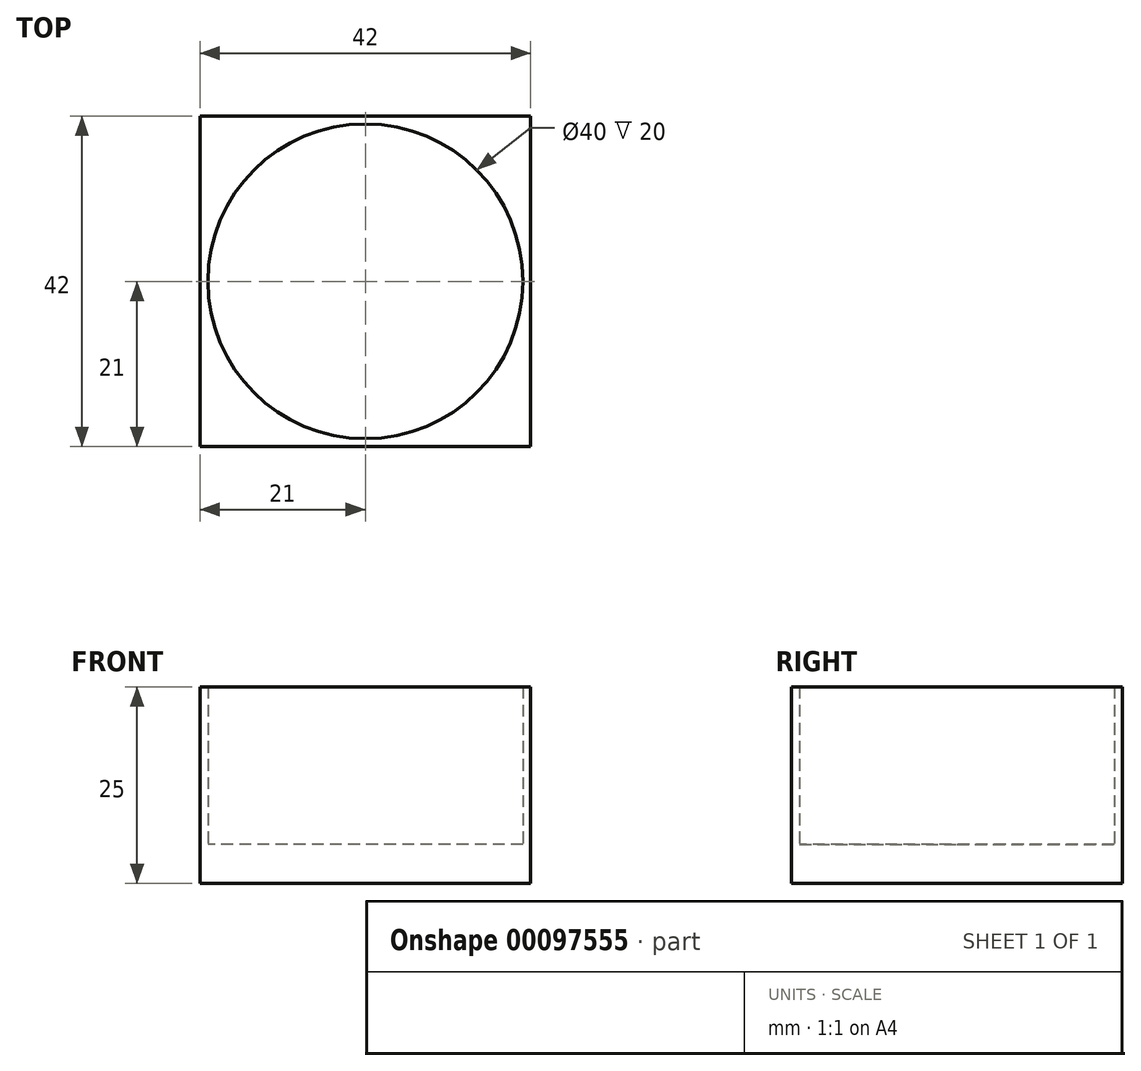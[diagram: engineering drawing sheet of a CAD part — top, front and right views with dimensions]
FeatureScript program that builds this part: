
annotation { "Feature Type Name" : "Feature", "Feature Type Description" : "" }
export const myFeature = defineFeature(function(context is Context, id is Id, definition is map)
    precondition{}
    {
        {
            var Q0;
            Q0=qCreatedBy(makeId("Top.planeOp"),FACE);
            var sketch = newSketch(context, id + "F0", { "sketchPlane" : qUnion([Q0])});
            skCircle(sketch, "E0", {"center": v(0, 0) * mm, "radius": 20 * mm});
            skLineSegment(sketch, "E1.bottom", {"start": v(0, 0) * mm, "end": v(-21, 0) * mm});
            skLineSegment(sketch, "E1.top", {"start": v(0, 0) * mm, "end": v(-21, 0) * mm});
            skLineSegment(sketch, "E1.left", {"start": v(0, 0) * mm, "end": v(0, 0) * mm});
            skLineSegment(sketch, "E1.right", {"start": v(-21, 0) * mm, "end": v(-21, 0) * mm});
            skLineSegment(sketch, "E2", {"start": v(-21, 0) * mm, "end": v(-21, 21) * mm});
            skLineSegment(sketch, "E3.bottom", {"start": v(-21, 21) * mm, "end": v(21, 21) * mm});
            skLineSegment(sketch, "E3.top", {"start": v(-21, -21) * mm, "end": v(21, -21) * mm});
            skLineSegment(sketch, "E3.left", {"start": v(-21, 21) * mm, "end": v(-21, -21) * mm});
            skLineSegment(sketch, "E3.right", {"start": v(21, 21) * mm, "end": v(21, -21) * mm});
            skSolve(sketch);
        }
        {
            var Q0;
            Q0=makeQuery(id+"F0.imprint","IMPRINT",FACE,{"disambiguationData":[TD([[makeQuery(id+"F0.imprint","IMPRINT",EDGE,{"derivedFrom":sQuery(id+"F0.wireOp",EDGE,"E0")}),1.0]])]});
            var Q1;
            Q1=makeQuery(id+"F0.imprint","IMPRINT",FACE,{"disambiguationData":[TD([[makeQuery(id+"F0.imprint","IMPRINT",EDGE,{"derivedFrom":sQuery(id+"F0.wireOp",EDGE,"E0")}),-1.0]])]});
            extrude(context, id + "F1", {"entities" : qUnion([Q0, Q1]), "depth" : 5 * mm});
        }
        {
            var Q0;
            Q0=makeQuery(id+"F0.imprint","IMPRINT",FACE,{"disambiguationData":[TD([[makeQuery(id+"F0.imprint","IMPRINT",EDGE,{"derivedFrom":sQuery(id+"F0.wireOp",EDGE,"E0")}),-1.0]])]});
            extrude(context, id + "F2", {"entities" : qUnion([Q0]), "operationType" : NewBodyOperationType.ADD, "depth" : 25 * mm});
        }
    });
